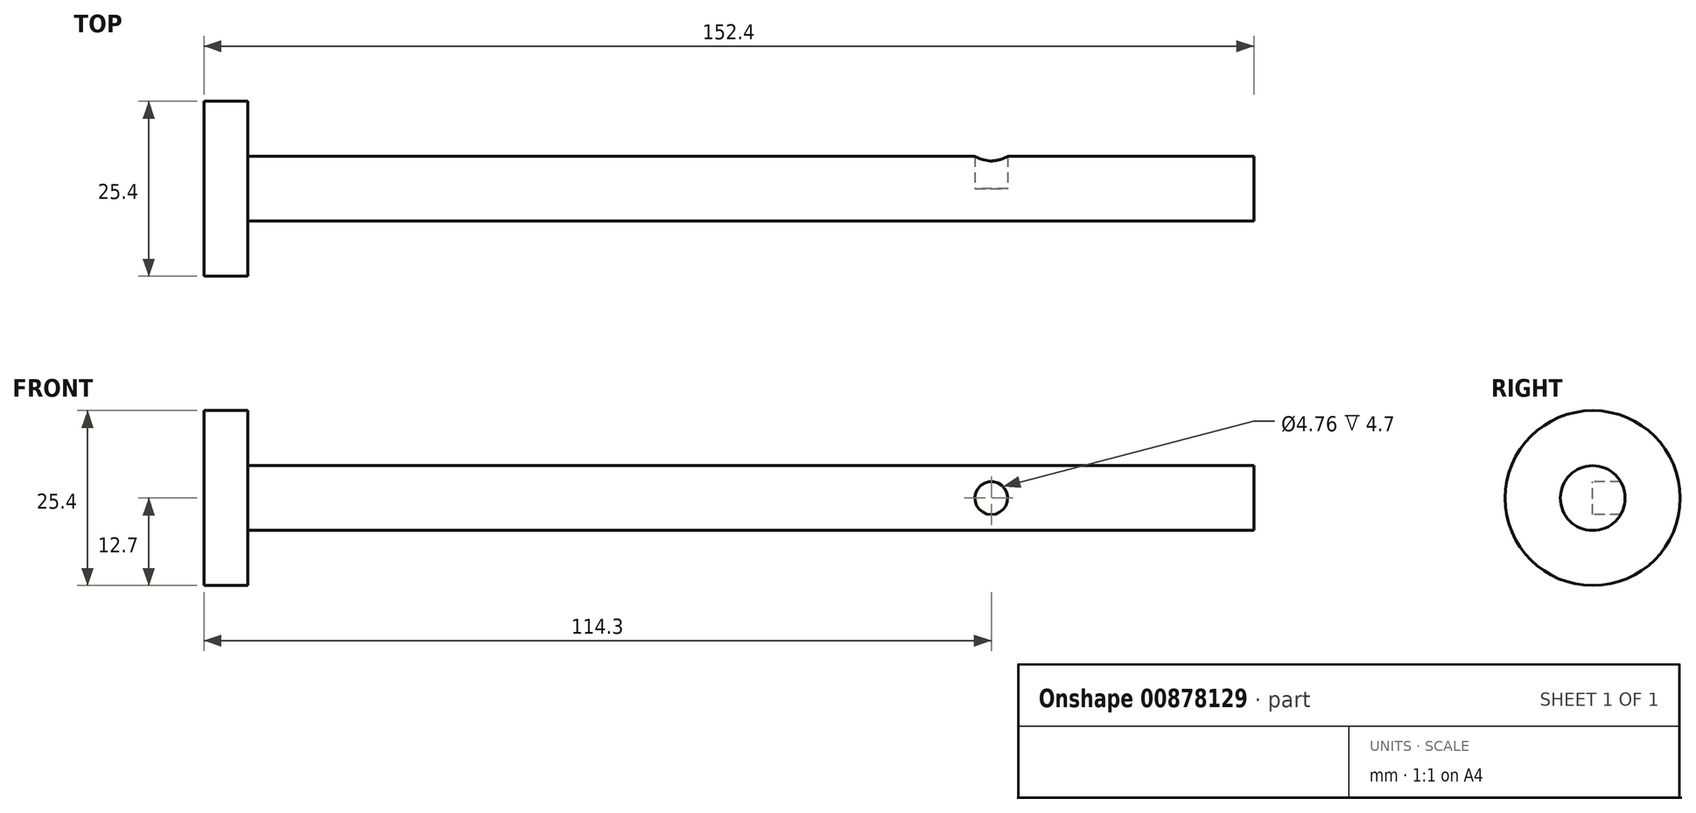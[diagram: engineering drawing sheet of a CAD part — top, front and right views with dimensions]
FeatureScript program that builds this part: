
annotation { "Feature Type Name" : "Feature", "Feature Type Description" : "" }
export const myFeature = defineFeature(function(context is Context, id is Id, definition is map)
    precondition{}
    {
        {
            var Q0;
            Q0=qCreatedBy(makeId("Right.planeOp"),FACE);
            var sketch = newSketch(context, id + "F0", { "sketchPlane" : qUnion([Q0])});
            skCircle(sketch, "E0", {"center": v(0, 0) * mm, "radius": 4.7 * mm});
            skSolve(sketch);
        }
        {
            var Q0;
            Q0=makeQuery(id+"F0.imprint","IMPRINT",FACE,{"disambiguationData":[TD([[makeQuery(id+"F0.imprint","IMPRINT",EDGE,{"derivedFrom":sQuery(id+"F0.wireOp",EDGE,"E0")}),1.0]])]});
            extrude(context, id + "F1", {"entities" : qUnion([Q0]), "depth" : 152.4 * mm, "offsetDistance" : 25.4 * mm});
        }
        {
            var Q0;
            Q0=qCreatedBy(makeId("Right.planeOp"),FACE);
            var sketch = newSketch(context, id + "F2", { "sketchPlane" : qUnion([Q0])});
            skCircle(sketch, "E1", {"center": v(0, 0) * mm, "radius": 12.7 * mm});
            skSolve(sketch);
        }
        {
            var Q0;
            Q0=makeQuery(id+"F2.imprint","IMPRINT",FACE,{"disambiguationData":[TD([[makeQuery(id+"F2.imprint","IMPRINT",EDGE,{"derivedFrom":sQuery(id+"F2.wireOp",EDGE,"E1")}),1.0]])]});
            extrude(context, id + "F3", {"entities" : qUnion([Q0]), "operationType" : NewBodyOperationType.ADD, "depth" : 6.35 * mm, "offsetDistance" : 25.4 * mm});
        }
        {
            var Q0;
            Q0=qCreatedBy(makeId("Front.planeOp"),FACE);
            var sketch = newSketch(context, id + "F4", { "sketchPlane" : qUnion([Q0])});
            skCircle(sketch, "E2", {"center": v(114.3, 0) * mm, "radius": 2.38 * mm});
            skSolve(sketch);
        }
        {
            var Q0;
            Q0 = qSketchRegion(id + "F4", true);
            extrude(context, id + "F5", {"entities" : qUnion([Q0]), "operationType" : NewBodyOperationType.REMOVE, "endBound" : BoundingType.THROUGH_ALL, "oppositeDirection" : true, "depth" : 25.4 * mm, "offsetDistance" : 25.4 * mm});
        }
    });
